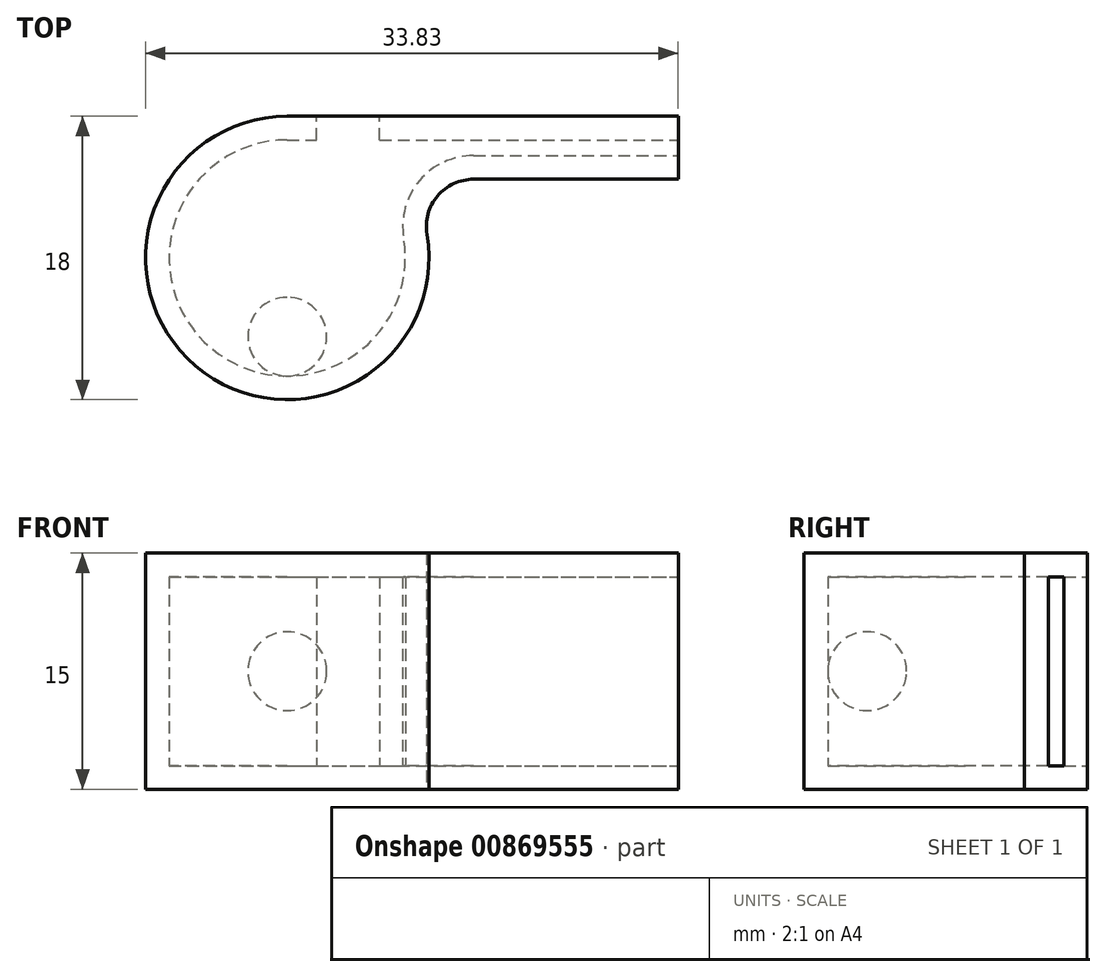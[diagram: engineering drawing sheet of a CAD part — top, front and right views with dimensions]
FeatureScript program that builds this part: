
annotation { "Feature Type Name" : "Feature", "Feature Type Description" : "" }
export const myFeature = defineFeature(function(context is Context, id is Id, definition is map)
    precondition{}
    {
        {
            var Q0;
            Q0=qCreatedBy(makeId("Top.planeOp"),FACE);
            var sketch = newSketch(context, id + "F0", { "sketchPlane" : qUnion([Q0])});
            skArc(sketch, "E0", {"start": v(0, 9) * mm, "mid": v(-5.8, -6.87) * mm, "end": v(8.87, 1.5) * mm});
            skLineSegment(sketch, "E1", {"start": v(0, 9) * mm, "end": v(24.83, 9) * mm});
            skLineSegment(sketch, "E2", {"start": v(24.83, 9) * mm, "end": v(24.83, 5) * mm});
            skLineSegment(sketch, "E3", {"start": v(11.83, 5) * mm, "end": v(24.83, 5) * mm});
            skPoint(sketch, "E4.visualSharp", {"position": v(7.48, 5) * mm});
            skArc(sketch, "E4.filletArc", {"start": v(11.83, 5) * mm, "mid": v(9.54, 3.94) * mm, "end": v(8.87, 1.5) * mm});
            skSolve(sketch);
        }
        {
            var Q0;
            Q0=makeQuery(id+"F0.imprint","IMPRINT",FACE,{"disambiguationData":[TD([[makeQuery(id+"F0.imprint","IMPRINT",EDGE,{"derivedFrom":sQuery(id+"F0.wireOp",EDGE,"E0")}),1.0]])]});
            extrude(context, id + "F1", {"entities" : qUnion([Q0]), "endBound" : BoundingType.SYMMETRIC, "depth" : 15 * mm, "offsetDistance" : 25 * mm});
        }
        {
            var Q0;
            Q0=makeQuery(id+"F1.opExtrude","SWEPT_FACE",FACE,{"disambiguationData":[OSD([sQuery(id+"F0.wireOp",EDGE,"E2")])]});
            shell(context, id + "F2", {"entities" : qUnion([Q0]), "thickness" : 1.5 * mm});
        }
        {
            var Q0;
            Q0=makeQuery(id+"F1.opExtrude","SWEPT_FACE",FACE,{"disambiguationData":[OSD([sQuery(id+"F0.wireOp",EDGE,"E1")])]});
            var sketch = newSketch(context, id + "F3", { "sketchPlane" : qUnion([Q0])});
            skLineSegment(sketch, "E5.bottom", {"start": v(-1.87, 6) * mm, "end": v(-5.87, 6) * mm});
            skLineSegment(sketch, "E5.top", {"start": v(-1.87, -6) * mm, "end": v(-5.87, -6) * mm});
            skLineSegment(sketch, "E5.left", {"start": v(-1.87, 6) * mm, "end": v(-1.87, -6) * mm});
            skLineSegment(sketch, "E5.right", {"start": v(-5.87, 6) * mm, "end": v(-5.87, -6) * mm});
            skSolve(sketch);
        }
        {
            var Q0;
            Q0 = qSketchRegion(id + "F3", true);
            extrude(context, id + "F4", {"entities" : qUnion([Q0]), "operationType" : NewBodyOperationType.REMOVE, "oppositeDirection" : true, "depth" : 1.5 * mm, "offsetDistance" : 25 * mm});
        }
        {
            var Q0;
            Q0=qCreatedBy(makeId("Top.planeOp"),FACE);
            var sketch = newSketch(context, id + "F5", { "sketchPlane" : qUnion([Q0])});
            skArc(sketch, "E6", {"start": v(0, -2.5) * mm, "mid": v(-2.5, -5) * mm, "end": v(0, -7.5) * mm});
            skLineSegment(sketch, "E7", {"start": v(0, -2.5) * mm, "end": v(0, -7.5) * mm});
            skSolve(sketch);
        }
        {
            var Q0;
            Q0 = qSketchRegion(id + "F5", true);
            var Q1;
            Q1=sQuery(id+"F5.wireOp",EDGE,"E7");
            revolve(context, id + "F6", {"surfaceOperationType" : NewSurfaceOperationType.NEW, "entities" : qUnion([Q0]), "axis" : qUnion([Q1]), "revolveType" : RevolveType.FULL});
        }
    });
